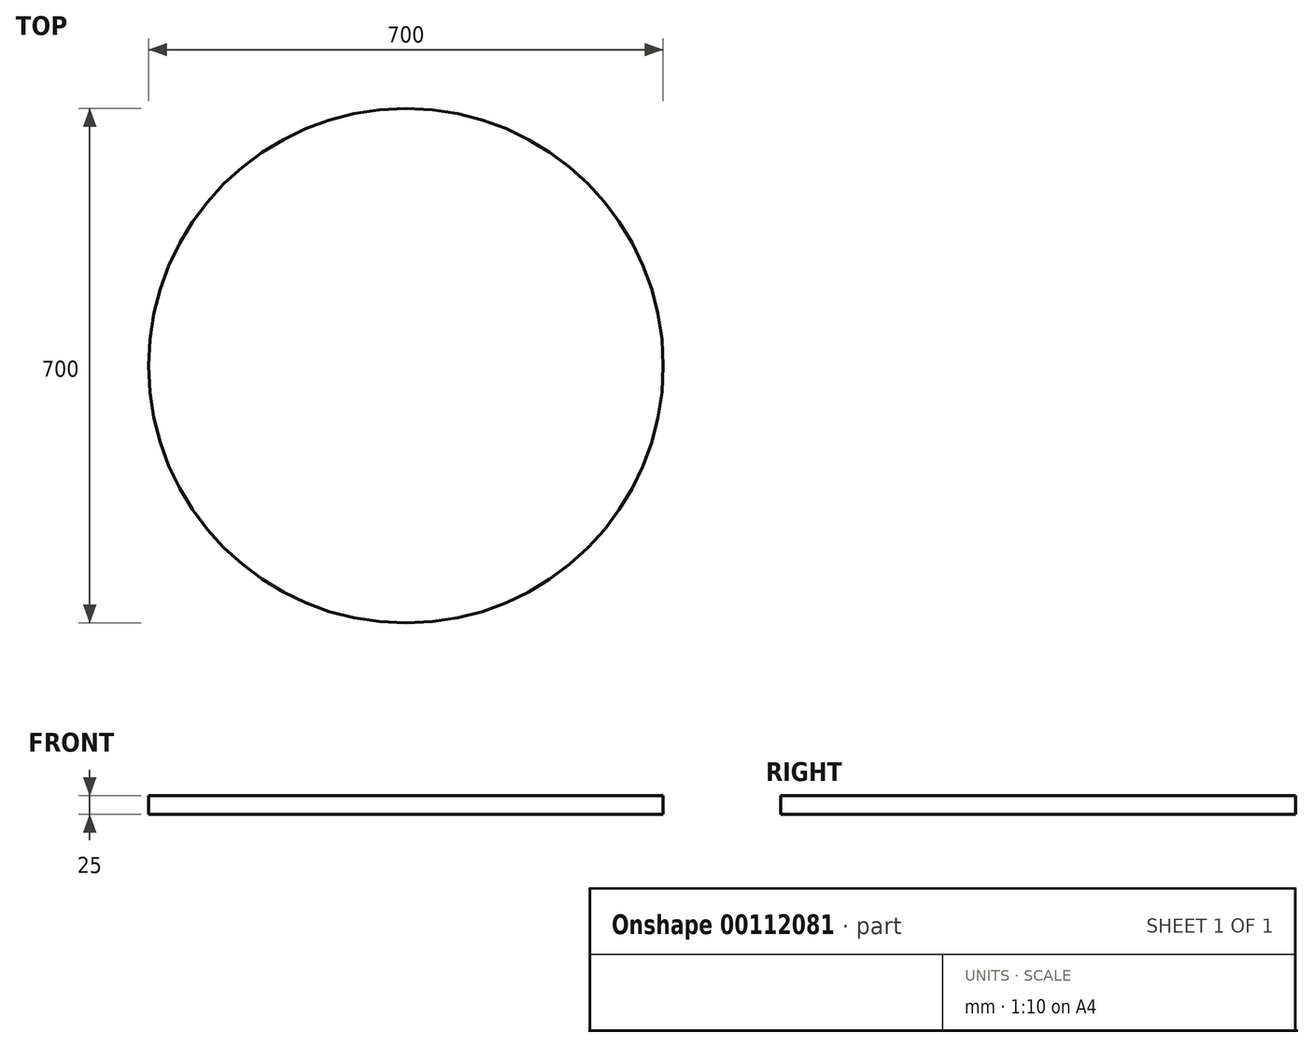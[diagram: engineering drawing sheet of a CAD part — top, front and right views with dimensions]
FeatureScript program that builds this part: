
annotation { "Feature Type Name" : "Feature", "Feature Type Description" : "" }
export const myFeature = defineFeature(function(context is Context, id is Id, definition is map)
    precondition{}
    {
        {
            var Q0;
            Q0=qCreatedBy(makeId("Top.planeOp"),FACE);
            var sketch = newSketch(context, id + "F0", { "sketchPlane" : qUnion([Q0])});
            skCircle(sketch, "E0", {"center": v(0, 0) * mm, "radius": 350 * mm});
            skSolve(sketch);
        }
        {
            var Q0;
            Q0 = qSketchRegion(id + "F0", true);
            extrude(context, id + "F1", {"entities" : qUnion([Q0]), "oppositeDirection" : true, "depth" : 25 * mm});
        }
    });
